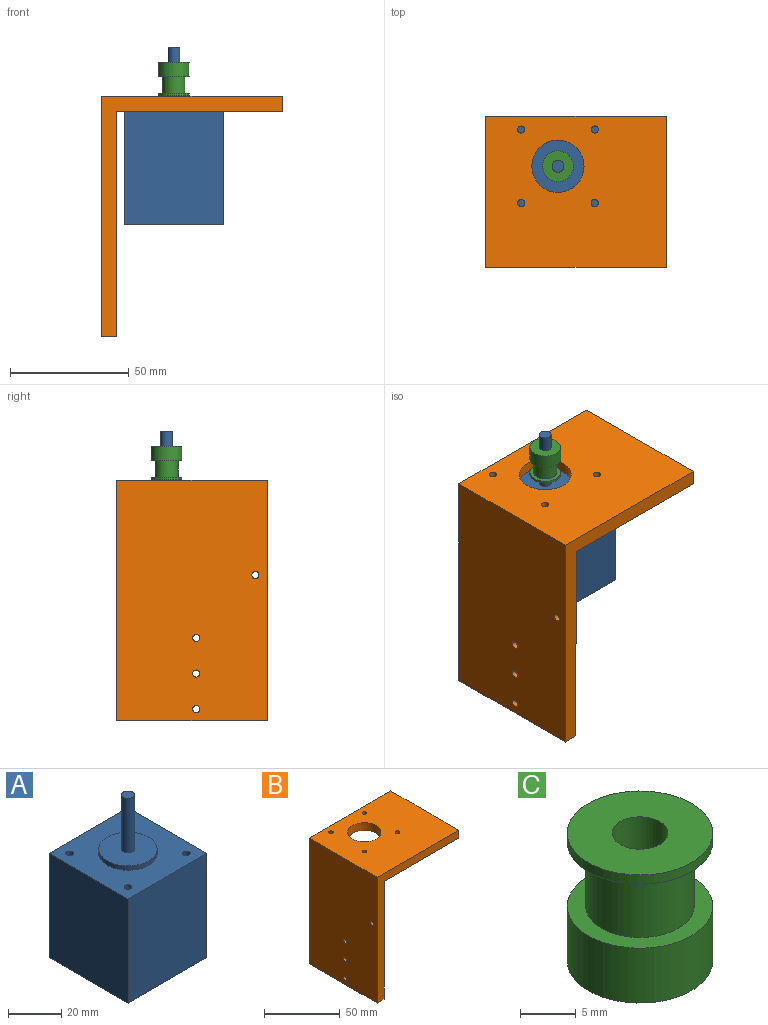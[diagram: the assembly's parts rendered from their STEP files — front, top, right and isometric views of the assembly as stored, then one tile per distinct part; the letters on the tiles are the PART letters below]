
ASSEMBLY  parts=3 mates=4
PART A: 18 faces, bbox 42x42x75 mm
  f0: plane 48x42mm, normal (1,0,0), area 2016mm2, adj f1,f3,f4,f5
  f1: plane 48x42mm, normal (0,1,0), area 2016mm2, adj f0,f2,f4,f5
  f2: plane 48x42mm, normal (-1,0,0), area 2016mm2, adj f1,f3,f4,f5
  f3: plane 48x42mm, normal (0,-1,0), area 2016mm2, adj f0,f2,f4,f5
  f4: plane 42x42mm, normal (0,0,1), area 1355.6mm2, adj f0,f1,f2,f3,f6,f10,f12,f14
  f5: plane 42x42mm, normal (0,0,-1), area 1764mm2, adj f0,f1,f2,f3
  f6: cylinder r=11mm len=22mm, axis (0,0,-1), area 138.2mm2, adj f4,f7
  f7: plane 22x22mm, normal (0,0,1), area 360.5mm2, adj f6,f8
  f8: cylinder r=2.5mm len=25mm, axis (0,0,-1), area 392.7mm2, adj f7,f9
  f9: plane 5x5mm, normal (0,0,1), area 19.6mm2, adj f8
  f10: cylinder r=1.5mm len=10mm, axis (0,0,1), area 94.2mm2, adj f4,f11
  f11: plane 3x3mm, normal (0,0,1), area 7.1mm2, adj f10
  f12: cylinder r=1.5mm len=10mm, axis (0,0,1), area 94.2mm2, adj f4,f13
  f13: plane 3x3mm, normal (0,0,1), area 7.1mm2, adj f12
  f14: cylinder r=1.5mm len=10mm, axis (0,0,1), area 94.2mm2, adj f4,f15
  f15: plane 3x3mm, normal (0,0,1), area 7.1mm2, adj f14
  f16: cylinder r=1.5mm len=10mm, axis (0,0,1), area 94.2mm2, adj f4,f17
  f17: plane 3x3mm, normal (0,0,1), area 7.1mm2, adj f16
PART B: 17 faces, bbox 76.2x63.5x101.6 mm
  f0: cylinder r=1.5mm len=6.35mm, axis (1,0,0), area 59.8mm2, adj f2,f4
  f1: cylinder r=1.5mm len=6.35mm, axis (1,0,0), area 59.8mm2, adj f2,f4
  f2: plane 101.6x63.5mm, normal (-1,0,0), area 6423.3mm2, adj f0,f1,f3,f7,f8,f9,f15,f16
  f3: plane 63.5x6.35mm, normal (0,0,-1), area 403.2mm2, adj f2,f4,f8,f9
  f4: plane 95.25x63.5mm, normal (1,0,0), area 6020.1mm2, adj f0,f1,f3,f5,f8,f9,f15,f16
  f5: plane 69.85x63.5mm, normal (0,0,-1), area 4027.1mm2, adj f4,f6,f8,f9,f10,f11,f12,f13
  f6: plane 63.5x6.35mm, normal (1,0,0), area 403.2mm2, adj f5,f7,f8,f9
  f7: plane 76.2x63.5mm, normal (0,0,1), area 4430.3mm2, adj f2,f6,f8,f9,f10,f11,f12,f13
  f8: plane 101.6x76.2mm, normal (0,-1,0), area 1088.7mm2, adj f2,f3,f4,f5,f6,f7
  f9: plane 101.6x76.2mm, normal (0,1,0), area 1088.7mm2, adj f2,f3,f4,f5,f6,f7
  f10: cylinder r=11mm len=22mm, axis (0,0,1), area 438.9mm2, adj f5,f7
  f11: cylinder r=1.5mm len=6.35mm, axis (0,0,1), area 59.8mm2, adj f5,f7
  f12: cylinder r=1.5mm len=6.35mm, axis (0,0,1), area 59.8mm2, adj f5,f7
  f13: cylinder r=1.5mm len=6.35mm, axis (0,0,1), area 59.8mm2, adj f5,f7
  f14: cylinder r=1.5mm len=6.35mm, axis (0,0,1), area 59.8mm2, adj f5,f7
  f15: cylinder r=1.5mm len=6.35mm, axis (1,0,0), area 59.8mm2, adj f2,f4
  f16: cylinder r=1.5mm len=6.35mm, axis (1,0,0), area 59.8mm2, adj f2,f4
PART C: 8 faces, bbox 13x13x14 mm
  f0: plane 13x13mm, normal (0,0,-1), area 113.1mm2, adj f1,f7
  f1: cylinder r=2.5mm len=14mm, axis (0,0,-1), area 219.9mm2, adj f0,f2
  f2: plane 13x13mm, normal (0,0,1), area 113.1mm2, adj f1,f3
  f3: cylinder r=6.5mm len=13mm, axis (0,0,-1), area 40.8mm2, adj f2,f4
  f4: plane 13x13mm, normal (0,0,-1), area 58.8mm2, adj f3,f5
  f5: cylinder r=4.85mm len=9.7mm, axis (0,0,-1), area 213.3mm2, adj f4,f6
  f6: plane 13x13mm, normal (0,0,1), area 58.8mm2, adj f5,f7
  f7: cylinder r=6.5mm len=13mm, axis (0,0,-1), area 245mm2, adj f0,f6
PLACE A t=(-41.21,16,-29.17)mm
PLACE B t=(-71.71,37,-76.42)mm
PLACE C rot(axis=(1,0,0),180deg) t=(-41.21,16,39.33)mm
MATE cylindrical A.f6 <-> B.f10  axis (0,0,1) through (-41.21,16,20.83)mm
MATE cylindrical A.f12 <-> B.f14  axis (0,0,1) through (-25.71,0.5,18.83)mm
MATE planar B.f5 <-> A.f6  axis (0,0,-1) through (4.49,5.25,18.83)mm
MATE cylindrical C.f1 <-> A.f8  axis (0,0,1) through (-41.21,16,33.33)mm
